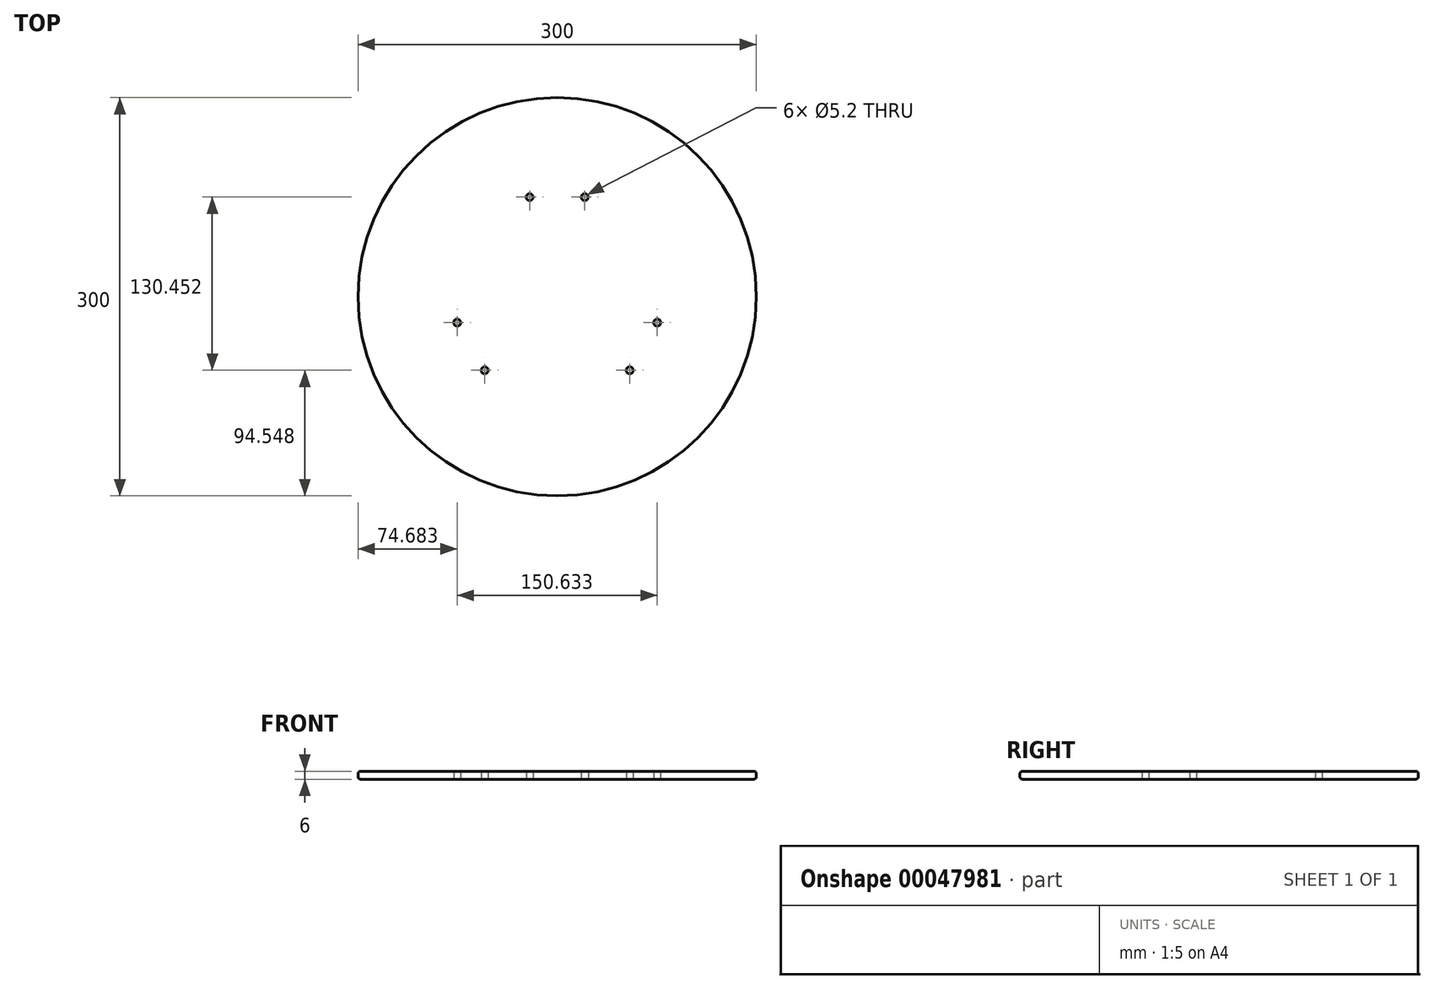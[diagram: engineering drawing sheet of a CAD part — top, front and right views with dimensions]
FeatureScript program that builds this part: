
annotation { "Feature Type Name" : "Feature", "Feature Type Description" : "" }
export const myFeature = defineFeature(function(context is Context, id is Id, definition is map)
    precondition{}
    {
        {
            assignVariable(context, id + "F0", {"name" : "bodyThickness", "anyValue" : 6});
        }
        {
            var Q0;
            Q0=qCreatedBy(makeId("Top.planeOp"),FACE);
            var sketch = newSketch(context, id + "F1", { "sketchPlane" : qUnion([Q0])});
            skCircle(sketch, "E0", {"center": v(0, 0) * mm, "radius": 150 * mm});
            skLineSegment(sketch, "E1", {"start": v(0, 150) * mm, "end": v(0, 0) * mm, "construction": true});
            skLineSegment(sketch, "E2", {"start": v(0, -150) * mm, "end": v(0, 0) * mm, "construction": true});
            skLineSegment(sketch, "E3", {"start": v(-150, 0) * mm, "end": v(0, 0) * mm, "construction": true});
            skLineSegment(sketch, "E4", {"start": v(0, 0) * mm, "end": v(150, 0) * mm, "construction": true});
            skCircle(sketch, "E5", {"center": v(-20.73, 75) * mm, "radius": 2.6 * mm});
            skCircle(sketch, "E6", {"center": v(20.73, 75) * mm, "radius": 2.6 * mm});
            skCircle(sketch, "E7", {"center": v(0, 0) * mm, "radius": 75 * mm, "construction": true});
            skLineSegment(sketch, "E8", {"start": v(-20.73, 75) * mm, "end": v(20.73, 75) * mm, "construction": true});
            skPoint(sketch, "E9", {"position": v(0, 75) * mm});
            skCircle(sketch, "E10.1.0", {"center": v(-75.32, -19.55) * mm, "radius": 2.6 * mm});
            skCircle(sketch, "E10.1.1", {"center": v(-54.59, -55.45) * mm, "radius": 2.6 * mm});
            skLineSegment(sketch, "E10.1.2", {"start": v(-54.59, -55.45) * mm, "end": v(-75.32, -19.55) * mm, "construction": true});
            skPoint(sketch, "E10.1.4", {"position": v(-64.95, -37.5) * mm});
            skCircle(sketch, "E10.2.0", {"center": v(54.59, -55.45) * mm, "radius": 2.6 * mm});
            skCircle(sketch, "E10.2.1", {"center": v(75.32, -19.55) * mm, "radius": 2.6 * mm});
            skLineSegment(sketch, "E10.2.2", {"start": v(75.32, -19.55) * mm, "end": v(54.59, -55.45) * mm, "construction": true});
            skPoint(sketch, "E10.2.4", {"position": v(64.95, -37.5) * mm});
            skSolve(sketch);
        }
        {
            var Q0;
            Q0=makeQuery(id+"F1.imprint","IMPRINT",FACE,{"disambiguationData":[TD([[makeQuery(id+"F1.imprint","IMPRINT",EDGE,{"derivedFrom":sQuery(id+"F1.wireOp",EDGE,"E0")}),1.0]])]});
            extrude(context, id + "F2", {"entities" : qUnion([Q0]), "depth" : (getVariable(context, 'bodyThickness')) * mm});
        }
        {
            var Q0;
            Q0=makeQuery(id+"F2.opExtrude","CAP_EDGE",EDGE,{"disambiguationData":[OSD([sQuery(id+"F1.wireOp",EDGE,"E0")])],"isStart":false});
            var Q1;
            Q1=makeQuery(id+"F2.opExtrude","CAP_EDGE",EDGE,{"disambiguationData":[OSD([sQuery(id+"F1.wireOp",EDGE,"E0")])],"isStart":true});
            fillet(context, id + "F3", {"entities" : qUnion([Q0, Q1]), "radius" : 2 * mm, "tangentPropagation" : true, "allowEdgeOverflow" : false});
        }
    });
